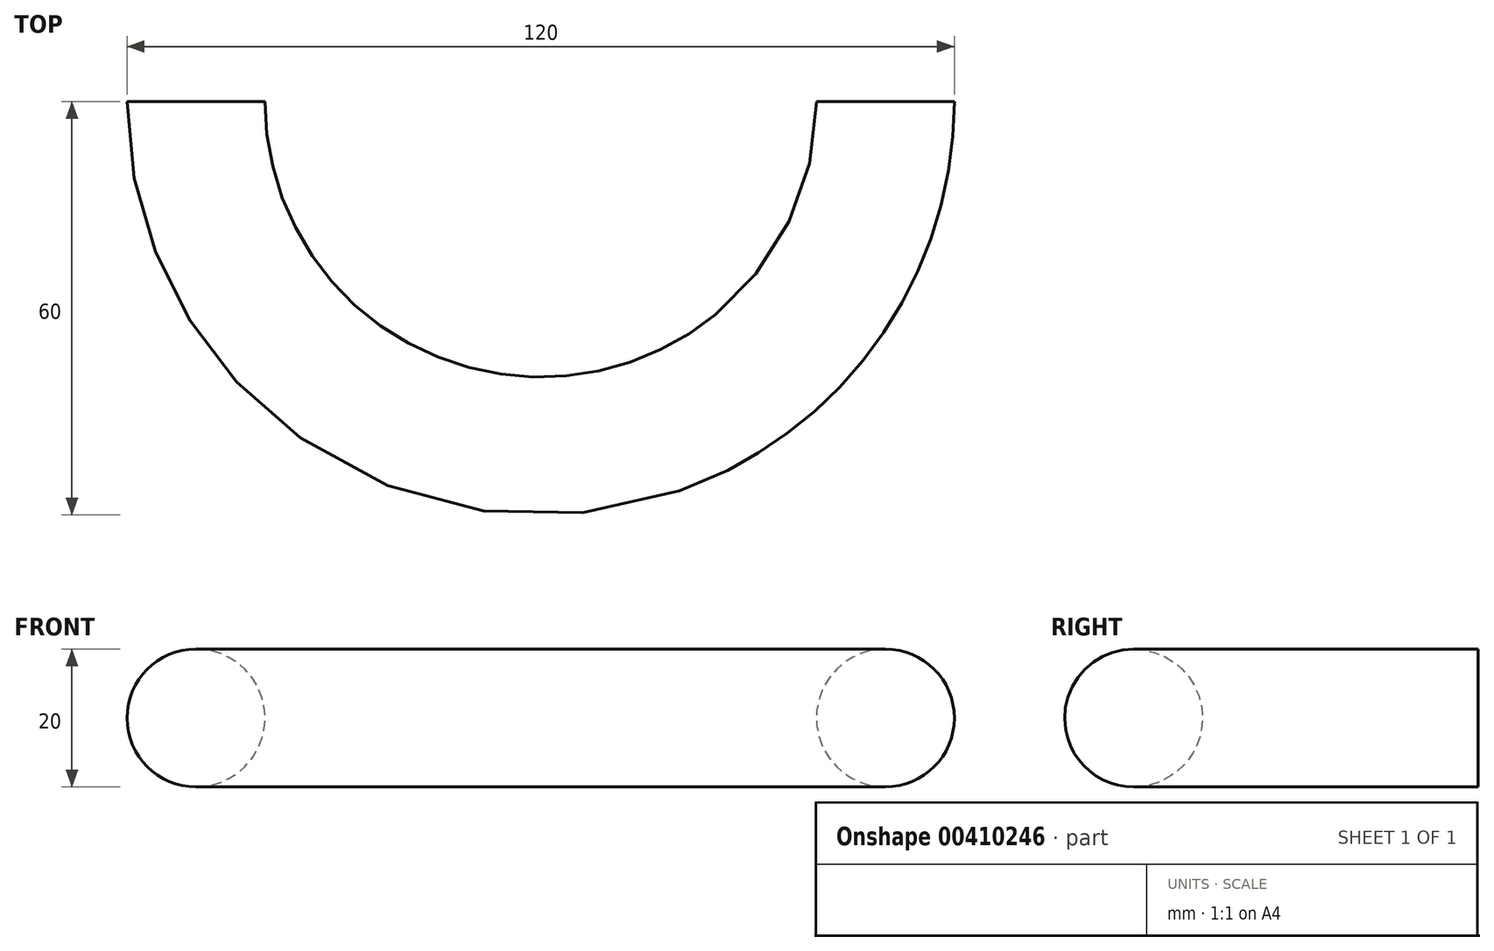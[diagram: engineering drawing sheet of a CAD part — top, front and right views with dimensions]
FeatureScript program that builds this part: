
annotation { "Feature Type Name" : "Feature", "Feature Type Description" : "" }
export const myFeature = defineFeature(function(context is Context, id is Id, definition is map)
    precondition{}
    {
        {
            var Q0;
            Q0=qCreatedBy(makeId("Front.planeOp"),FACE);
            var sketch = newSketch(context, id + "F0", { "sketchPlane" : qUnion([Q0])});
            skCircle(sketch, "E0", {"center": v(50, 0) * mm, "radius": 10 * mm});
            skLineSegment(sketch, "E1", {"start": v(0, 18.04) * mm, "end": v(0, -37.47) * mm});
            skSolve(sketch);
        }
        {
            var Q0;
            Q0=makeQuery(id+"F0.imprint","IMPRINT",FACE,{"disambiguationData":[TD([[makeQuery(id+"F0.imprint","IMPRINT",EDGE,{"derivedFrom":sQuery(id+"F0.wireOp",EDGE,"E0")}),1.0]])]});
            var Q1;
            Q1=sQuery(id+"F0.wireOp",EDGE,"E1");
            revolve(context, id + "F1", {"entities" : qUnion([Q0]), "axis" : qUnion([Q1]), "revolveType" : RevolveType.ONE_DIRECTION, "angle" : 180 * degree});
        }
    });
